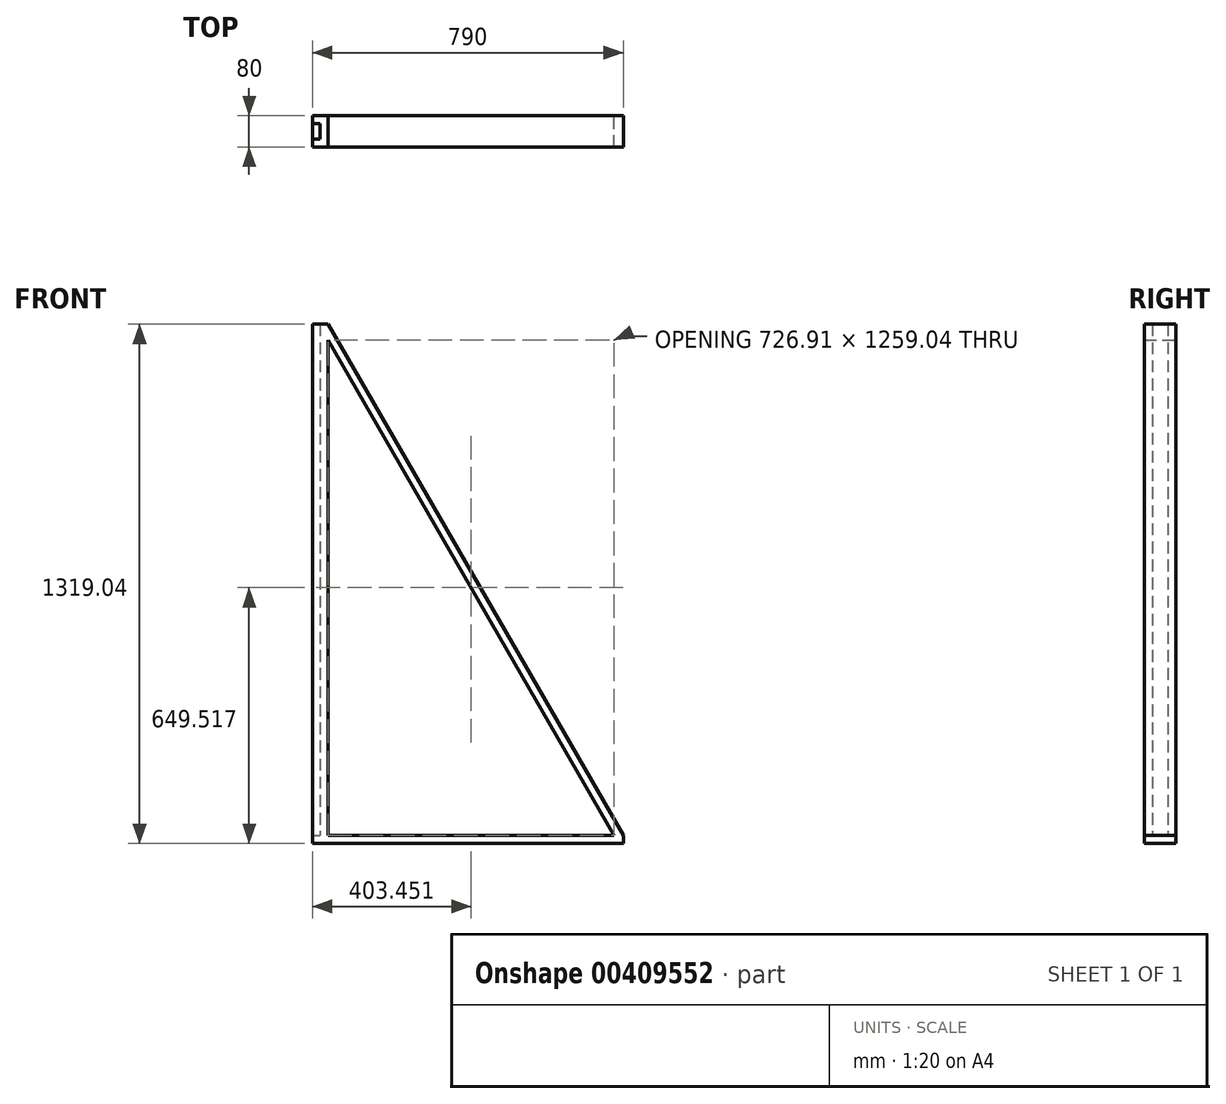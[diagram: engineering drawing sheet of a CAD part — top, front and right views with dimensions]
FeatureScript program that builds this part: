
annotation { "Feature Type Name" : "Feature", "Feature Type Description" : "" }
export const myFeature = defineFeature(function(context is Context, id is Id, definition is map)
    precondition{}
    {
        {
            var Q0;
            Q0=qCreatedBy(makeId("Front.planeOp"),FACE);
            var sketch = newSketch(context, id + "F0", { "sketchPlane" : qUnion([Q0])});
            skLineSegment(sketch, "E0.bottom", {"start": v(258.45, 1601.79) * mm, "end": v(298.45, 1601.79) * mm});
            skLineSegment(sketch, "E0.top", {"start": v(258.45, 302.75) * mm, "end": v(298.45, 302.75) * mm});
            skLineSegment(sketch, "E0.left", {"start": v(258.45, 1601.79) * mm, "end": v(258.45, 302.75) * mm});
            skLineSegment(sketch, "E0.right", {"start": v(298.45, 1561.79) * mm, "end": v(298.45, 302.75) * mm});
            skLineSegment(sketch, "E1.bottom", {"start": v(298.45, 302.75) * mm, "end": v(1048.45, 302.75) * mm});
            skLineSegment(sketch, "E1.top", {"start": v(258.45, 282.75) * mm, "end": v(1048.45, 282.75) * mm});
            skLineSegment(sketch, "E1.left", {"start": v(258.45, 302.75) * mm, "end": v(258.45, 282.75) * mm});
            skLineSegment(sketch, "E1.right", {"start": v(1048.45, 302.75) * mm, "end": v(1048.45, 282.75) * mm});
            skLineSegment(sketch, "E2", {"start": v(298.45, 1601.79) * mm, "end": v(1048.45, 302.75) * mm});
            skLineSegment(sketch, "E3", {"start": v(1025.35, 302.75) * mm, "end": v(298.45, 1561.79) * mm});
            skSolve(sketch);
        }
        {
            var Q0;
            Q0 = qSketchRegion(id + "F0", true);
            extrude(context, id + "F1", {"entities" : qUnion([Q0]), "depth" : 80 * mm, "offsetDistance" : 25 * mm});
        }
        {
            var Q0;
            Q0=makeQuery(id+"F1.opExtrude","SWEPT_FACE",FACE,{"disambiguationData":[OSD([sQuery(id+"F0.wireOp",EDGE,"E1.top")])]});
            var sketch = newSketch(context, id + "F2", { "sketchPlane" : qUnion([Q0])});
            skLineSegment(sketch, "E4.bottom", {"start": v(258.45, 60) * mm, "end": v(278.45, 60) * mm});
            skLineSegment(sketch, "E4.top", {"start": v(258.45, 20) * mm, "end": v(278.45, 20) * mm});
            skLineSegment(sketch, "E4.left", {"start": v(258.45, 60) * mm, "end": v(258.45, 20) * mm});
            skLineSegment(sketch, "E4.right", {"start": v(278.45, 60) * mm, "end": v(278.45, 20) * mm});
            skSolve(sketch);
        }
        {
            var Q0;
            Q0=makeQuery(id+"F2.imprint","IMPRINT",FACE,{"disambiguationData":[TD([[makeQuery(id+"F2.imprint","IMPRINT",EDGE,{"derivedFrom":sQuery(id+"F2.wireOp",EDGE,"E4.bottom")}),-1.0]])]});
            extrude(context, id + "F3", {"entities" : qUnion([Q0]), "operationType" : NewBodyOperationType.REMOVE, "endBound" : BoundingType.THROUGH_ALL, "oppositeDirection" : true, "depth" : 25 * mm, "offsetDistance" : 25 * mm, "hasSecondDirection" : true, "secondDirectionOppositeDirection" : true, "secondDirectionDepth" : 20 * mm});
        }
    });
